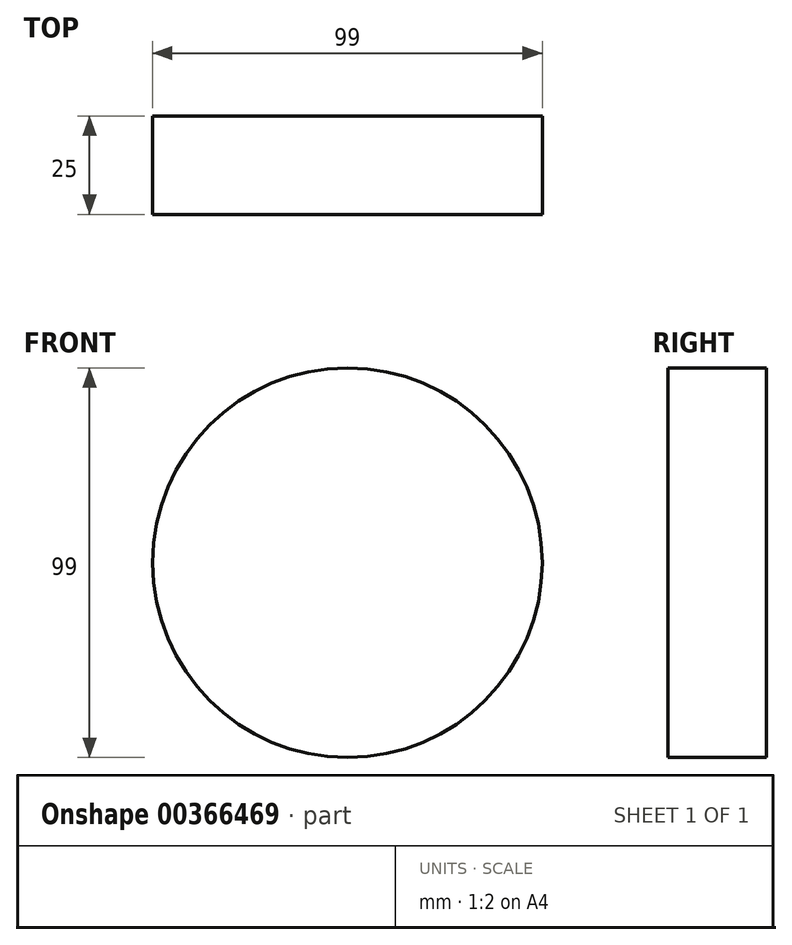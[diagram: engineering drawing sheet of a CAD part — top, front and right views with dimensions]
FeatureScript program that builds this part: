
annotation { "Feature Type Name" : "Feature", "Feature Type Description" : "" }
export const myFeature = defineFeature(function(context is Context, id is Id, definition is map)
    precondition{}
    {
        {
            var Q0;
            Q0=qCreatedBy(makeId("Front.planeOp"),FACE);
            var sketch = newSketch(context, id + "F0", { "sketchPlane" : qUnion([Q0])});
            skCircle(sketch, "E0", {"center": v(0, 0) * mm, "radius": 49.5 * mm});
            skSolve(sketch);
        }
        {
            var Q0;
            Q0 = qSketchRegion(id + "F0", true);
            extrude(context, id + "F1", {"entities" : qUnion([Q0]), "depth" : 25 * mm});
        }
    });
